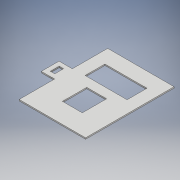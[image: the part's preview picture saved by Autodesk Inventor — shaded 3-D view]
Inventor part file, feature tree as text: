
AUTODESK INVENTOR PART (.ipt)
format: ipt  version: 2017 (Build 210142000, 142)  size: 123,392 bytes
history: native  units: mm
features: extrude x2, sketch x2
ambient origin geometry x8: Origin, YZ Plane, XZ Plane, XY Plane, X Axis, Y Axis, Z Axis, Center Point
bodies: Solid1 (feature_tree)
feature tree (4):
  extrude  "Extrusion1"  Depth=3.0mm TaperAngle=0.0deg
  extrude  "Extrusion2"  Depth=10.0mm
  sketch  "Sketch1"  dims[d0=150.0mm d23=3.0mm d24=0.0mm]
  sketch  "Sketch2"  dims[d35=10.0mm d45=10.0mm d47=3.0mm d48=0.0mm d49=200.0mm d50=40.0mm d51=80.0mm d52=10.0mm d53=95.0mm d54=45.0mm d55=45.0mm d56=55.0mm d41=10.0mm d42=10.0mm]
